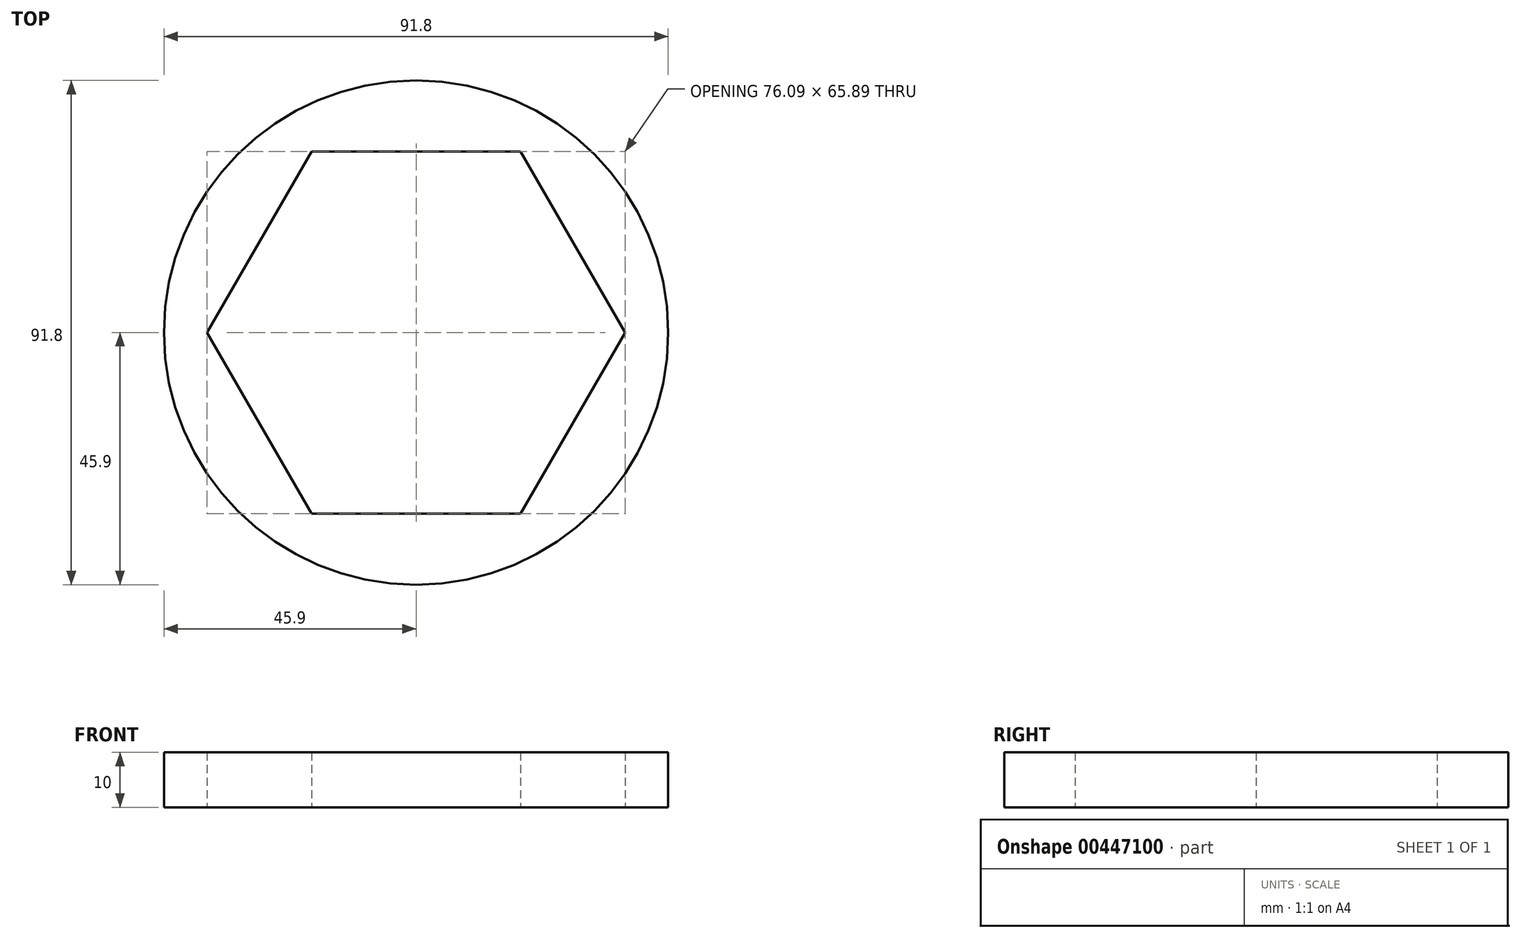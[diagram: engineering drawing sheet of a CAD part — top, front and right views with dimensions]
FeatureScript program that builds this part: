
annotation { "Feature Type Name" : "Feature", "Feature Type Description" : "" }
export const myFeature = defineFeature(function(context is Context, id is Id, definition is map)
    precondition{}
    {
        {
            var Q0;
            Q0=qCreatedBy(makeId("Top.planeOp"),FACE);
            var sketch = newSketch(context, id + "F0", { "sketchPlane" : qUnion([Q0])});
            skCircle(sketch, "E0", {"center": v(0, 0) * mm, "radius": 45.9 * mm});
            skCircle(sketch, "E1.cCircle", {"center": v(0, 0) * mm, "radius": 38.04 * mm, "construction": true});
            skLineSegment(sketch, "E1.0", {"start": v(-38.04, 0) * mm, "end": v(-19.02, 32.95) * mm});
            skLineSegment(sketch, "E1.1", {"start": v(-19.02, 32.95) * mm, "end": v(19.02, 32.95) * mm});
            skLineSegment(sketch, "E1.2", {"start": v(19.02, 32.95) * mm, "end": v(38.04, 0) * mm});
            skLineSegment(sketch, "E1.3", {"start": v(38.04, 0) * mm, "end": v(19.02, -32.95) * mm});
            skLineSegment(sketch, "E1.4", {"start": v(19.02, -32.95) * mm, "end": v(-19.02, -32.95) * mm});
            skLineSegment(sketch, "E1.5", {"start": v(-19.02, -32.95) * mm, "end": v(-38.04, 0) * mm});
            skSolve(sketch);
        }
        {
            var Q0;
            Q0=makeQuery(id+"F0.imprint","IMPRINT",FACE,{"disambiguationData":[TD([[makeQuery(id+"F0.imprint","IMPRINT",EDGE,{"derivedFrom":sQuery(id+"F0.wireOp",EDGE,"E0")}),1.0]])]});
            extrude(context, id + "F1", {"entities" : qUnion([Q0]), "depth" : 10 * mm});
        }
    });
